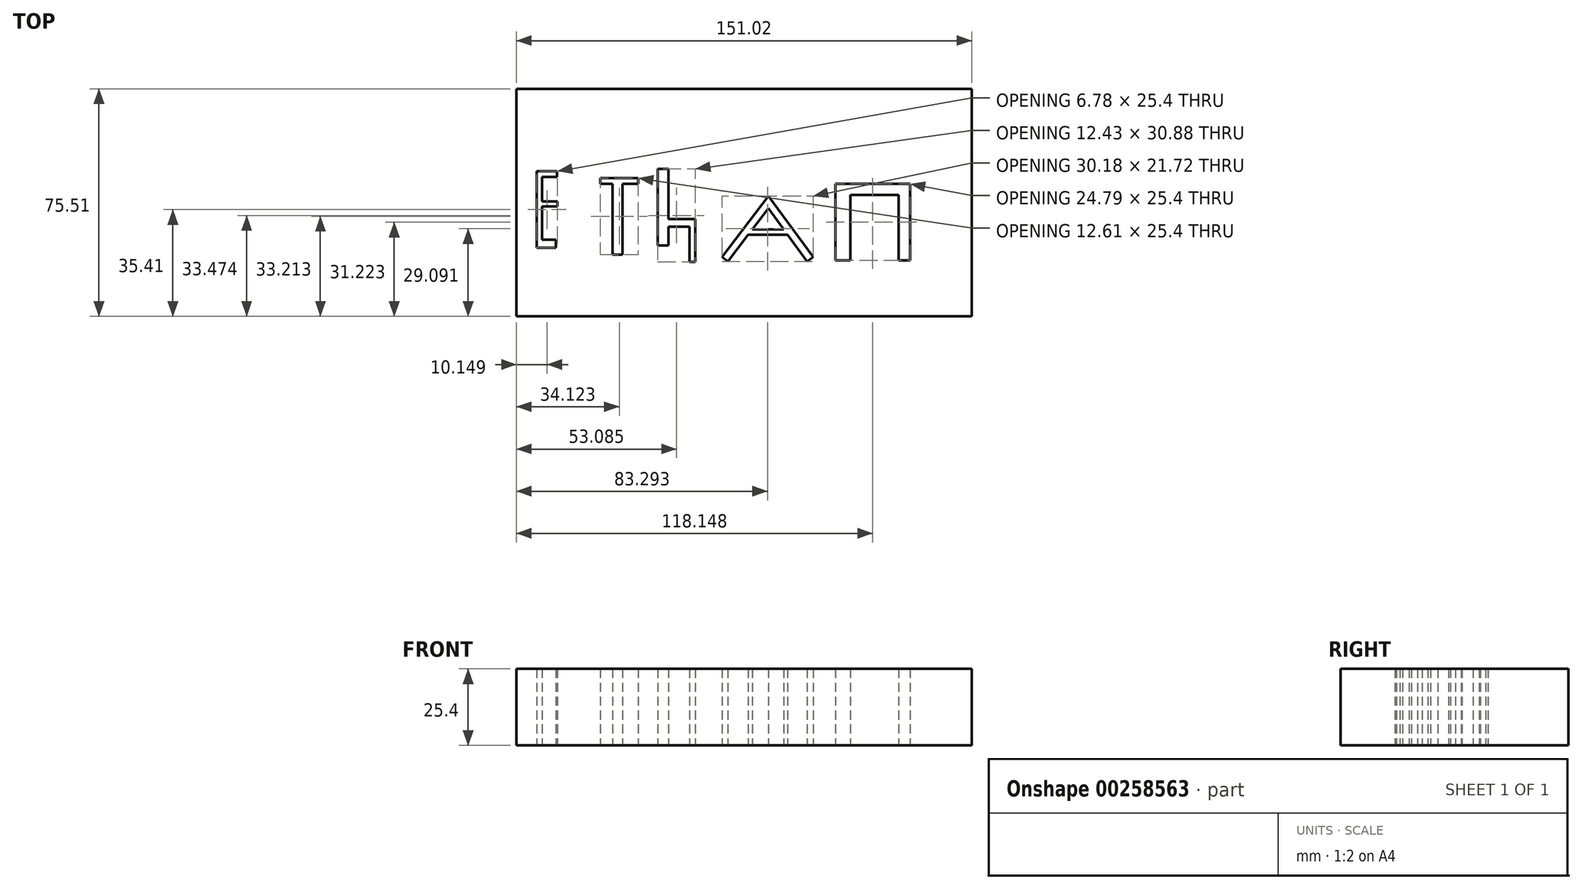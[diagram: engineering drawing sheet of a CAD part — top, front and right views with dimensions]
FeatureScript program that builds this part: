
annotation { "Feature Type Name" : "Feature", "Feature Type Description" : "" }
export const myFeature = defineFeature(function(context is Context, id is Id, definition is map)
    precondition{}
    {
        {
            var Q0;
            Q0=qCreatedBy(makeId("Top.planeOp"),FACE);
            var sketch = newSketch(context, id + "F0", { "sketchPlane" : qUnion([Q0])});
            skLineSegment(sketch, "E0.bottom", {"start": v(-74.68, 75.51) * mm, "end": v(76.34, 75.51) * mm});
            skLineSegment(sketch, "E0.top", {"start": v(-74.68, 0) * mm, "end": v(76.34, 0) * mm});
            skLineSegment(sketch, "E0.left", {"start": v(-74.68, 75.51) * mm, "end": v(-74.68, 0) * mm});
            skLineSegment(sketch, "E0.right", {"start": v(76.34, 75.51) * mm, "end": v(76.34, 0) * mm});
            skLineSegment(sketch, "E1.bottom", {"start": v(-67.92, 48.1) * mm, "end": v(-66.19, 48.1) * mm});
            skLineSegment(sketch, "E1.top", {"start": v(-67.92, 22.7) * mm, "end": v(-66.19, 22.7) * mm});
            skLineSegment(sketch, "E1.left", {"start": v(-67.92, 48.1) * mm, "end": v(-67.92, 22.7) * mm});
            skLineSegment(sketch, "E1.right", {"start": v(-66.19, 48.1) * mm, "end": v(-66.19, 22.7) * mm});
            skLineSegment(sketch, "E2.bottom", {"start": v(-66.19, 48.1) * mm, "end": v(-61.22, 48.1) * mm});
            skLineSegment(sketch, "E2.top", {"start": v(-66.19, 46.3) * mm, "end": v(-61.22, 46.3) * mm});
            skLineSegment(sketch, "E2.left", {"start": v(-66.19, 48.1) * mm, "end": v(-66.19, 46.3) * mm});
            skLineSegment(sketch, "E2.right", {"start": v(-61.22, 48.1) * mm, "end": v(-61.22, 46.3) * mm});
            skLineSegment(sketch, "E3.bottom", {"start": v(-66.19, 38.1) * mm, "end": v(-61.14, 38.1) * mm});
            skLineSegment(sketch, "E3.top", {"start": v(-66.19, 36.44) * mm, "end": v(-61.14, 36.44) * mm});
            skLineSegment(sketch, "E3.left", {"start": v(-66.19, 38.1) * mm, "end": v(-66.19, 36.44) * mm});
            skLineSegment(sketch, "E3.right", {"start": v(-61.14, 38.1) * mm, "end": v(-61.14, 36.44) * mm});
            skLineSegment(sketch, "E4.bottom", {"start": v(-66.19, 25.47) * mm, "end": v(-61.61, 25.47) * mm});
            skLineSegment(sketch, "E4.top", {"start": v(-66.19, 22.7) * mm, "end": v(-61.61, 22.7) * mm});
            skLineSegment(sketch, "E4.left", {"start": v(-66.19, 25.47) * mm, "end": v(-66.19, 22.7) * mm});
            skLineSegment(sketch, "E4.right", {"start": v(-61.61, 25.47) * mm, "end": v(-61.61, 22.7) * mm});
            skLineSegment(sketch, "E5.bottom", {"start": v(-42.75, 43.95) * mm, "end": v(-39.48, 43.95) * mm});
            skLineSegment(sketch, "E5.top", {"start": v(-42.75, 20.51) * mm, "end": v(-39.48, 20.51) * mm});
            skLineSegment(sketch, "E5.left", {"start": v(-42.75, 43.95) * mm, "end": v(-42.75, 20.51) * mm});
            skLineSegment(sketch, "E5.right", {"start": v(-39.48, 43.95) * mm, "end": v(-39.48, 20.51) * mm});
            skLineSegment(sketch, "E6.bottom", {"start": v(-46.86, 43.95) * mm, "end": v(-34.25, 43.95) * mm});
            skLineSegment(sketch, "E6.top", {"start": v(-46.86, 45.91) * mm, "end": v(-34.25, 45.91) * mm});
            skLineSegment(sketch, "E6.left", {"start": v(-46.86, 43.95) * mm, "end": v(-46.86, 45.91) * mm});
            skLineSegment(sketch, "E6.right", {"start": v(-34.25, 43.95) * mm, "end": v(-34.25, 45.91) * mm});
            skLineSegment(sketch, "E7.bottom", {"start": v(-27.8, 48.91) * mm, "end": v(-24.24, 48.91) * mm});
            skLineSegment(sketch, "E7.top", {"start": v(-27.8, 23.51) * mm, "end": v(-24.24, 23.51) * mm});
            skLineSegment(sketch, "E7.left", {"start": v(-27.8, 48.91) * mm, "end": v(-27.8, 23.51) * mm});
            skLineSegment(sketch, "E7.right", {"start": v(-24.24, 48.91) * mm, "end": v(-24.24, 23.51) * mm});
            skLineSegment(sketch, "E8.bottom", {"start": v(-24.24, 32.27) * mm, "end": v(-17.22, 32.27) * mm});
            skLineSegment(sketch, "E8.top", {"start": v(-24.24, 29.78) * mm, "end": v(-17.22, 29.78) * mm});
            skLineSegment(sketch, "E8.left", {"start": v(-24.24, 32.27) * mm, "end": v(-24.24, 29.78) * mm});
            skLineSegment(sketch, "E8.right", {"start": v(-17.22, 32.27) * mm, "end": v(-17.22, 29.78) * mm});
            skLineSegment(sketch, "E9.bottom", {"start": v(-17.22, 32.27) * mm, "end": v(-15.38, 32.27) * mm});
            skLineSegment(sketch, "E9.top", {"start": v(-17.22, 18.03) * mm, "end": v(-15.38, 18.03) * mm});
            skLineSegment(sketch, "E9.left", {"start": v(-17.22, 32.27) * mm, "end": v(-17.22, 18.03) * mm});
            skLineSegment(sketch, "E9.right", {"start": v(-15.38, 32.27) * mm, "end": v(-15.38, 18.03) * mm});
            skLineSegment(sketch, "E10", {"start": v(-6.48, 19.7) * mm, "end": v(8.86, 39.95) * mm});
            skLineSegment(sketch, "E11", {"start": v(8.86, 39.95) * mm, "end": v(8.86, 35.82) * mm});
            skLineSegment(sketch, "E12", {"start": v(8.86, 35.82) * mm, "end": v(-4.6, 18.23) * mm});
            skLineSegment(sketch, "E13", {"start": v(-4.6, 18.23) * mm, "end": v(-6.48, 19.7) * mm});
            skLineSegment(sketch, "E14", {"start": v(8.86, 39.95) * mm, "end": v(23.7, 19.7) * mm});
            skLineSegment(sketch, "E15", {"start": v(8.86, 35.82) * mm, "end": v(21.76, 18.23) * mm});
            skLineSegment(sketch, "E16", {"start": v(21.76, 18.23) * mm, "end": v(23.7, 19.7) * mm});
            skLineSegment(sketch, "E17", {"start": v(3.54, 28.87) * mm, "end": v(13.96, 28.87) * mm});
            skLineSegment(sketch, "E18", {"start": v(13.96, 28.87) * mm, "end": v(15.3, 27.03) * mm});
            skLineSegment(sketch, "E19", {"start": v(15.3, 27.03) * mm, "end": v(2.13, 27.03) * mm});
            skLineSegment(sketch, "E20", {"start": v(2.13, 27.03) * mm, "end": v(3.54, 28.87) * mm});
            skLineSegment(sketch, "E21.bottom", {"start": v(31.07, 18.52) * mm, "end": v(36.13, 18.52) * mm});
            skLineSegment(sketch, "E21.top", {"start": v(31.07, 43.92) * mm, "end": v(36.13, 43.92) * mm});
            skLineSegment(sketch, "E21.left", {"start": v(31.07, 18.52) * mm, "end": v(31.07, 43.92) * mm});
            skLineSegment(sketch, "E21.right", {"start": v(36.13, 18.52) * mm, "end": v(36.13, 43.92) * mm});
            skLineSegment(sketch, "E22.bottom", {"start": v(36.13, 43.92) * mm, "end": v(52.02, 43.92) * mm});
            skLineSegment(sketch, "E22.top", {"start": v(36.13, 40.28) * mm, "end": v(52.02, 40.28) * mm});
            skLineSegment(sketch, "E22.left", {"start": v(36.13, 43.92) * mm, "end": v(36.13, 40.28) * mm});
            skLineSegment(sketch, "E22.right", {"start": v(52.02, 43.92) * mm, "end": v(52.02, 40.28) * mm});
            skLineSegment(sketch, "E23.bottom", {"start": v(52.02, 43.92) * mm, "end": v(55.86, 43.92) * mm});
            skLineSegment(sketch, "E23.top", {"start": v(52.02, 18.52) * mm, "end": v(55.86, 18.52) * mm});
            skLineSegment(sketch, "E23.left", {"start": v(52.02, 43.92) * mm, "end": v(52.02, 18.52) * mm});
            skLineSegment(sketch, "E23.right", {"start": v(55.86, 43.92) * mm, "end": v(55.86, 18.52) * mm});
            skSolve(sketch);
        }
        {
            var Q0;
            Q0=makeQuery(id+"F0.imprint","IMPRINT",FACE,{"disambiguationData":[TD([[makeQuery(id+"F0.imprint","IMPRINT",EDGE,{"derivedFrom":sQuery(id+"F0.wireOp",EDGE,"E0.bottom")}),-1.0]])]});
            var Q1;
            {var subQ3=sQuery(id+"F0.wireOp",EDGE,"E17");Q1=makeQuery(id+"F0.imprint","IMPRINT",FACE,{"disambiguationData":[TD([[makeQuery(id+"F0.imprint","IMPRINT",EDGE,{"derivedFrom":subQ3}),1.0]])]});}
            extrude(context, id + "F1", {"entities" : qUnion([Q0, Q1]), "depth" : 25.4 * mm});
        }
    });
